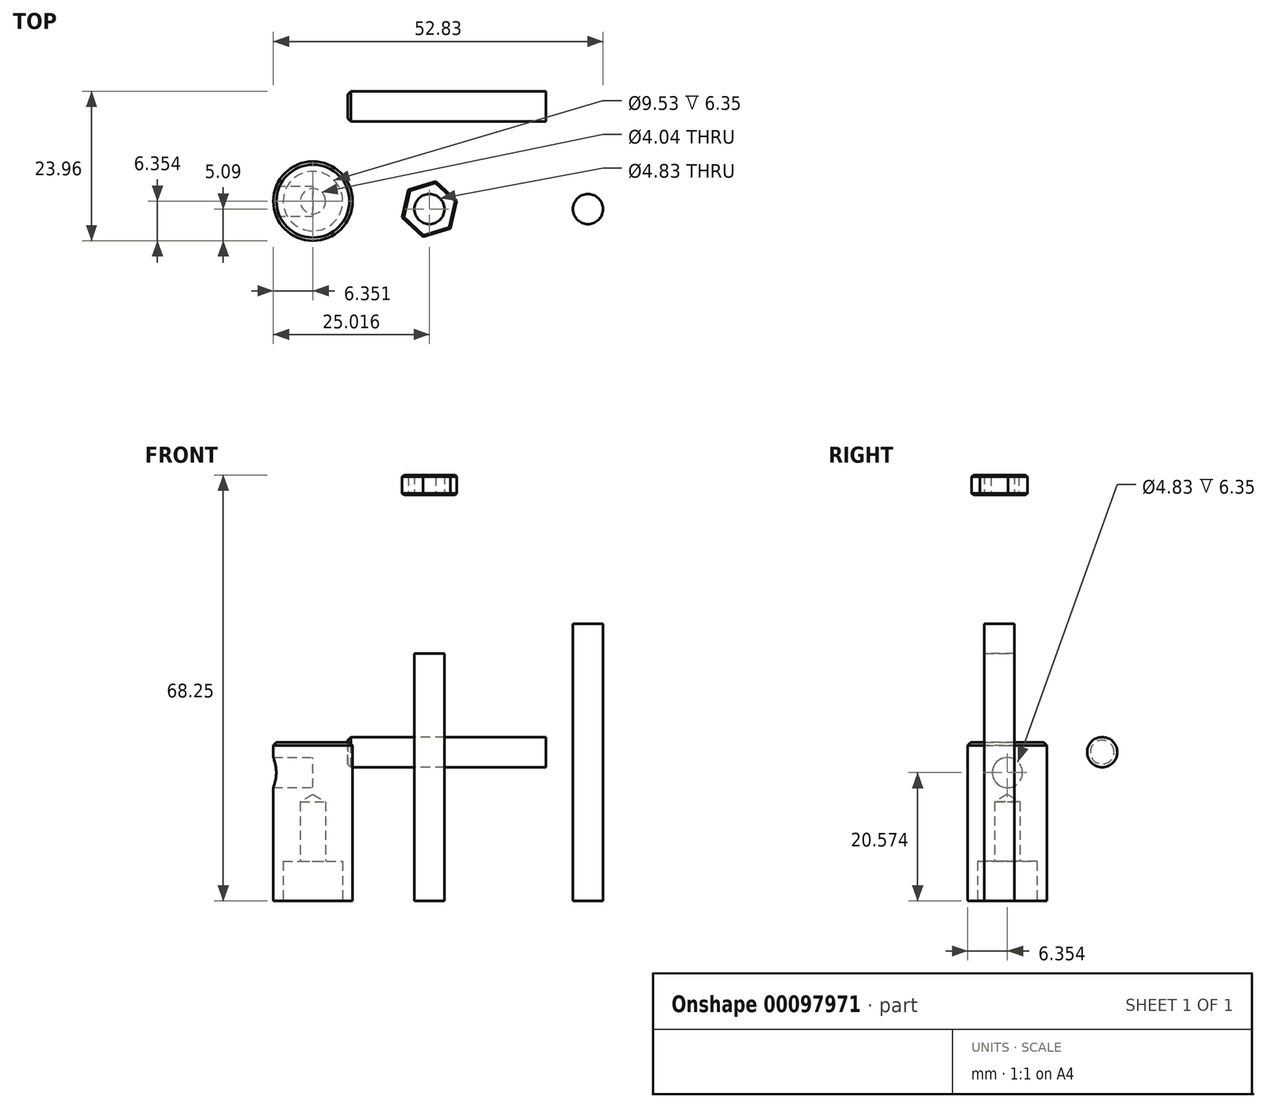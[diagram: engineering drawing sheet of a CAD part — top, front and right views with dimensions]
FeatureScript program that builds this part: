
annotation { "Feature Type Name" : "Feature", "Feature Type Description" : "" }
export const myFeature = defineFeature(function(context is Context, id is Id, definition is map)
    precondition{}
    {
        {
            var Q0;
            Q0=qCreatedBy(makeId("Top.planeOp"),FACE);
            var sketch = newSketch(context, id + "F0", { "sketchPlane" : qUnion([Q0])});
            skCircle(sketch, "E0", {"center": v(13.12, 0) * mm, "radius": 2.41 * mm});
            skSolve(sketch);
        }
        {
            var Q0;
            Q0=makeQuery(id+"F0.imprint","IMPRINT",FACE,{"disambiguationData":[TD([[makeQuery(id+"F0.imprint","IMPRINT",EDGE,{"derivedFrom":sQuery(id+"F0.wireOp",EDGE,"E0")}),1.0]])]});
            extrude(context, id + "F1", {"entities" : qUnion([Q0]), "depth" : 39.67 * mm});
        }
        {
            var Q0;
            Q0=makeQuery(id+"F1.opExtrude","SWEPT_BODY",BODY,{"disambiguationData":[OSD([sQuery(id+"F0.wireOp",EDGE,"E0")])]});
            var Q1;
            Q1=qCreatedBy(makeId("Right.planeOp"),FACE);
            transform(context, id + "F2", {"entities" : qUnion([Q0]), "transformType" : TransformType.TRANSLATION_DISTANCE, "transformDirection" : qUnion([Q1]), "distance" : 25.4 * mm, "makeCopy" : true});
        }
        {
            var Q0;
            Q0=makeQuery(id+"F2.opPattern","COPY",FACE,{"derivedFrom":makeQuery(id+"F1.opExtrude","CAP_FACE",FACE,{"disambiguationData":[OSD([sQuery(id+"F0.wireOp",EDGE,"E0")])],"isStart":false}),"instanceName":"1"});
            extrude(context, id + "F3", {"entities" : qUnion([Q0]), "operationType" : NewBodyOperationType.ADD, "depth" : 4.75 * mm});
        }
        {
            var Q0;
            Q0=makeQuery(id+"F1.opExtrude","CAP_FACE",FACE,{"disambiguationData":[OSD([sQuery(id+"F0.wireOp",EDGE,"E0")])],"isStart":false});
            cPlane(context, id + "F4", {"entities" : qUnion([Q0]), "cplaneType" : CPlaneType.OFFSET, "offset" : 25.4 * mm, "width" : 152.4 * mm, "height" : 152.4 * mm});
        }
        {
            var Q0;
            Q0=qCreatedBy(id+"F4.planeOp",FACE);
            var sketch = newSketch(context, id + "F5", { "sketchPlane" : qUnion([Q0])});
            skCircle(sketch, "E1.0", {"center": v(13.12, 0) * mm, "radius": 2.41 * mm, "construction": true});
            skCircle(sketch, "E2.cCircle", {"center": v(13.12, 0) * mm, "radius": 3.96 * mm, "construction": true});
            skLineSegment(sketch, "E2.0", {"start": v(8.74, -1.35) * mm, "end": v(9.76, 3.11) * mm});
            skLineSegment(sketch, "E2.1", {"start": v(9.76, 3.11) * mm, "end": v(14.14, 4.46) * mm});
            skLineSegment(sketch, "E2.2", {"start": v(14.14, 4.46) * mm, "end": v(17.49, 1.35) * mm});
            skLineSegment(sketch, "E2.3", {"start": v(17.49, 1.35) * mm, "end": v(16.47, -3.11) * mm});
            skLineSegment(sketch, "E2.4", {"start": v(16.47, -3.11) * mm, "end": v(12.1, -4.46) * mm});
            skLineSegment(sketch, "E2.5", {"start": v(12.1, -4.46) * mm, "end": v(8.74, -1.35) * mm});
            skPoint(sketch, "E2.0.midPoint", {"position": v(9.25, 0.88) * mm});
            skCircle(sketch, "E3", {"center": v(13.12, 0) * mm, "radius": 2.41 * mm});
            skSolve(sketch);
        }
        {
            var Q0;
            Q0=makeQuery(id+"F5.imprint","IMPRINT",FACE,{"disambiguationData":[TD([[makeQuery(id+"F5.imprint","IMPRINT",EDGE,{"derivedFrom":sQuery(id+"F5.wireOp",EDGE,"E2.0")}),-1.0]])]});
            extrude(context, id + "F6", {"entities" : qUnion([Q0]), "depth" : 3.17 * mm});
        }
        {
            var Q0;
            Q0=makeQuery(id+"F6.opExtrude","CAP_EDGE",EDGE,{"disambiguationData":[OSD([sQuery(id+"F5.wireOp",EDGE,"E2.0")])],"isStart":false});
            var Q1;
            Q1=makeQuery(id+"F6.opExtrude","CAP_EDGE",EDGE,{"disambiguationData":[OSD([sQuery(id+"F5.wireOp",EDGE,"E2.1")])],"isStart":false});
            var Q2;
            Q2=makeQuery(id+"F6.opExtrude","CAP_EDGE",EDGE,{"disambiguationData":[OSD([sQuery(id+"F5.wireOp",EDGE,"E2.2")])],"isStart":false});
            var Q3;
            Q3=makeQuery(id+"F6.opExtrude","CAP_EDGE",EDGE,{"disambiguationData":[OSD([sQuery(id+"F5.wireOp",EDGE,"E2.3")])],"isStart":false});
            var Q4;
            Q4=makeQuery(id+"F6.opExtrude","CAP_EDGE",EDGE,{"disambiguationData":[OSD([sQuery(id+"F5.wireOp",EDGE,"E2.4")])],"isStart":false});
            var Q5;
            Q5=makeQuery(id+"F6.opExtrude","CAP_EDGE",EDGE,{"disambiguationData":[OSD([sQuery(id+"F5.wireOp",EDGE,"E2.5")])],"isStart":false});
            var Q6;
            Q6=makeQuery(id+"F6.opExtrude","CAP_EDGE",EDGE,{"disambiguationData":[OSD([sQuery(id+"F5.wireOp",EDGE,"E2.2")])],"isStart":true});
            var Q7;
            Q7=makeQuery(id+"F6.opExtrude","CAP_EDGE",EDGE,{"disambiguationData":[OSD([sQuery(id+"F5.wireOp",EDGE,"E2.1")])],"isStart":true});
            var Q8;
            Q8=makeQuery(id+"F6.opExtrude","CAP_EDGE",EDGE,{"disambiguationData":[OSD([sQuery(id+"F5.wireOp",EDGE,"E2.0")])],"isStart":true});
            var Q9;
            Q9=makeQuery(id+"F6.opExtrude","CAP_EDGE",EDGE,{"disambiguationData":[OSD([sQuery(id+"F5.wireOp",EDGE,"E2.5")])],"isStart":true});
            var Q10;
            Q10=makeQuery(id+"F6.opExtrude","CAP_EDGE",EDGE,{"disambiguationData":[OSD([sQuery(id+"F5.wireOp",EDGE,"E2.4")])],"isStart":true});
            var Q11;
            Q11=makeQuery(id+"F6.opExtrude","CAP_EDGE",EDGE,{"disambiguationData":[OSD([sQuery(id+"F5.wireOp",EDGE,"E2.3")])],"isStart":true});
            chamfer(context, id + "F7", {"entities" : qUnion([Q0, Q1, Q2, Q3, Q4, Q5, Q6, Q7, Q8, Q9, Q10, Q11]), "width" : 0.25 * mm, "tangentPropagation" : true});
        }
        {
            var Q0;
            Q0=qCreatedBy(makeId("Top.planeOp"),FACE);
            var sketch = newSketch(context, id + "F8", { "sketchPlane" : qUnion([Q0])});
            skCircle(sketch, "E4", {"center": v(-5.55, 1.26) * mm, "radius": 6.35 * mm});
            skSolve(sketch);
        }
        {
            var Q0;
            Q0=makeQuery(id+"F8.imprint","IMPRINT",FACE,{"disambiguationData":[TD([[makeQuery(id+"F8.imprint","IMPRINT",EDGE,{"derivedFrom":sQuery(id+"F8.wireOp",EDGE,"E4")}),1.0]])]});
            extrude(context, id + "F9", {"entities" : qUnion([Q0]), "depth" : 25.4 * mm});
        }
        {
            var Q0;
            Q0=makeQuery(id+"F9.opExtrude","CAP_FACE",FACE,{"disambiguationData":[OSD([sQuery(id+"F8.wireOp",EDGE,"E4")])],"isStart":true});
            var sketch = newSketch(context, id + "F10", { "sketchPlane" : qUnion([Q0])});
            skCircle(sketch, "E5.0.0", {"center": v(-5.55, -1.26) * mm, "radius": 6.35 * mm, "construction": true});
            skCircle(sketch, "E6", {"center": v(-5.55, -1.26) * mm, "radius": 4.76 * mm});
            skSolve(sketch);
        }
        {
            var Q0;
            Q0=makeQuery(id+"F10.imprint","IMPRINT",FACE,{"disambiguationData":[TD([[makeQuery(id+"F10.imprint","IMPRINT",EDGE,{"derivedFrom":sQuery(id+"F10.wireOp",EDGE,"E6")}),1.0]])]});
            extrude(context, id + "F11", {"entities" : qUnion([Q0]), "operationType" : NewBodyOperationType.REMOVE, "oppositeDirection" : true, "depth" : 6.35 * mm});
        }
        {
            var Q0;
            Q0=makeQuery(id+"F11.boolean.opBoolean","COPY",FACE,{"derivedFrom":makeQuery(id+"F11.opExtrude","CAP_FACE",FACE,{"disambiguationData":[OSD([sQuery(id+"F10.wireOp",EDGE,"E6")])],"isStart":false})});
            var sketch = newSketch(context, id + "F12", { "sketchPlane" : qUnion([Q0])});
            skCircle(sketch, "E7.0.0", {"center": v(-5.55, -1.26) * mm, "radius": 4.76 * mm});
            skSolve(sketch);
        }
        {
            var Q0;
            Q0=sQuery(id+"F12.wireOp",VERTEX,"E7.0.0.center");
            var Q1;
            Q1=makeQuery(id+"F9.opExtrude","SWEPT_BODY",BODY,{"disambiguationData":[OSD([sQuery(id+"F8.wireOp",EDGE,"E4")])]});
            hole(context, id + "F13", {"style" : HoleStyle.SIMPLE, "endStyle" : HoleEndStyle.BLIND, "standardTappedOrClearance" : lookupTablePath({ "standard" : "ANSI", "engagement" : "75%", "pitch" : "32 tpi", "size" : "#10", "type" : "Tapped" }), "standardBlindInLast" : lookupTablePath({ "standard" : "ANSI", "engagement" : "75%", "pitch" : "32 tpi", "size" : "#10", "type" : "Tapped" }), "holeDiameter" : 4.04 * mm, "holeDepth" : 9.52 * mm, "locations" : qUnion([Q0]), "scope" : qUnion([Q1]), "majorDiameter" : 4.83 * mm});
        }
        {
            var Q0;
            Q0=makeQuery(id+"F9.opExtrude","CAP_EDGE",EDGE,{"disambiguationData":[OSD([sQuery(id+"F8.wireOp",EDGE,"E4")])],"isStart":false});
            cPlane(context, id + "F14", {"entities" : qUnion([Q0]), "cplaneType" : CPlaneType.LINE_ANGLE, "offset" : 152.4 * mm, "angle" : 0 * degree, "width" : 152.4 * mm, "height" : 152.4 * mm});
        }
        {
            var Q0;
            Q0=qCreatedBy(id+"F14.planeOp",FACE);
            var sketch = newSketch(context, id + "F15", { "sketchPlane" : qUnion([Q0])});
            skLineSegment(sketch, "E8", {"start": v(7.61, 25.4) * mm, "end": v(7.61, 0) * mm, "construction": true});
            skLineSegment(sketch, "E9.0", {"start": v(-5.09, 25.4) * mm, "end": v(7.61, 25.4) * mm, "construction": true});
            skLineSegment(sketch, "E10", {"start": v(-5.09, 0) * mm, "end": v(-5.09, 25.4) * mm, "construction": true});
            skLineSegment(sketch, "E11", {"start": v(7.61, 20.57) * mm, "end": v(-5.09, 20.57) * mm, "construction": true});
            skCircle(sketch, "E12", {"center": v(1.26, 20.57) * mm, "radius": 2.41 * mm});
            skSolve(sketch);
        }
        {
            var Q0;
            Q0 = qSketchRegion(id + "F15", true);
            extrude(context, id + "F16", {"entities" : qUnion([Q0]), "operationType" : NewBodyOperationType.REMOVE, "endBound" : BoundingType.THROUGH_ALL, "oppositeDirection" : true, "depth" : 25.4 * mm});
        }
        {
            var Q0;
            Q0=qCreatedBy(makeId("Right.planeOp"),FACE);
            var sketch = newSketch(context, id + "F17", { "sketchPlane" : qUnion([Q0])});
            skCircle(sketch, "E13", {"center": v(16.46, 23.85) * mm, "radius": 2.41 * mm});
            skSolve(sketch);
        }
        {
            var Q0;
            Q0=makeQuery(id+"F17.imprint","IMPRINT",FACE,{"disambiguationData":[TD([[makeQuery(id+"F17.imprint","IMPRINT",EDGE,{"derivedFrom":sQuery(id+"F17.wireOp",EDGE,"E13")}),1.0]])]});
            extrude(context, id + "F18", {"entities" : qUnion([Q0]), "depth" : 31.75 * mm});
        }
        {
            var Q0;
            Q0=makeQuery(id+"F18.opExtrude","CAP_EDGE",EDGE,{"disambiguationData":[OSD([sQuery(id+"F17.wireOp",EDGE,"E13")])],"isStart":true});
            var Q1;
            Q1=makeQuery(id+"F9.opExtrude","CAP_EDGE",EDGE,{"disambiguationData":[OSD([sQuery(id+"F8.wireOp",EDGE,"E4")])],"isStart":false});
            chamfer(context, id + "F19", {"entities" : qUnion([Q0, Q1]), "width" : 0.5 * mm, "tangentPropagation" : true});
        }
    });
